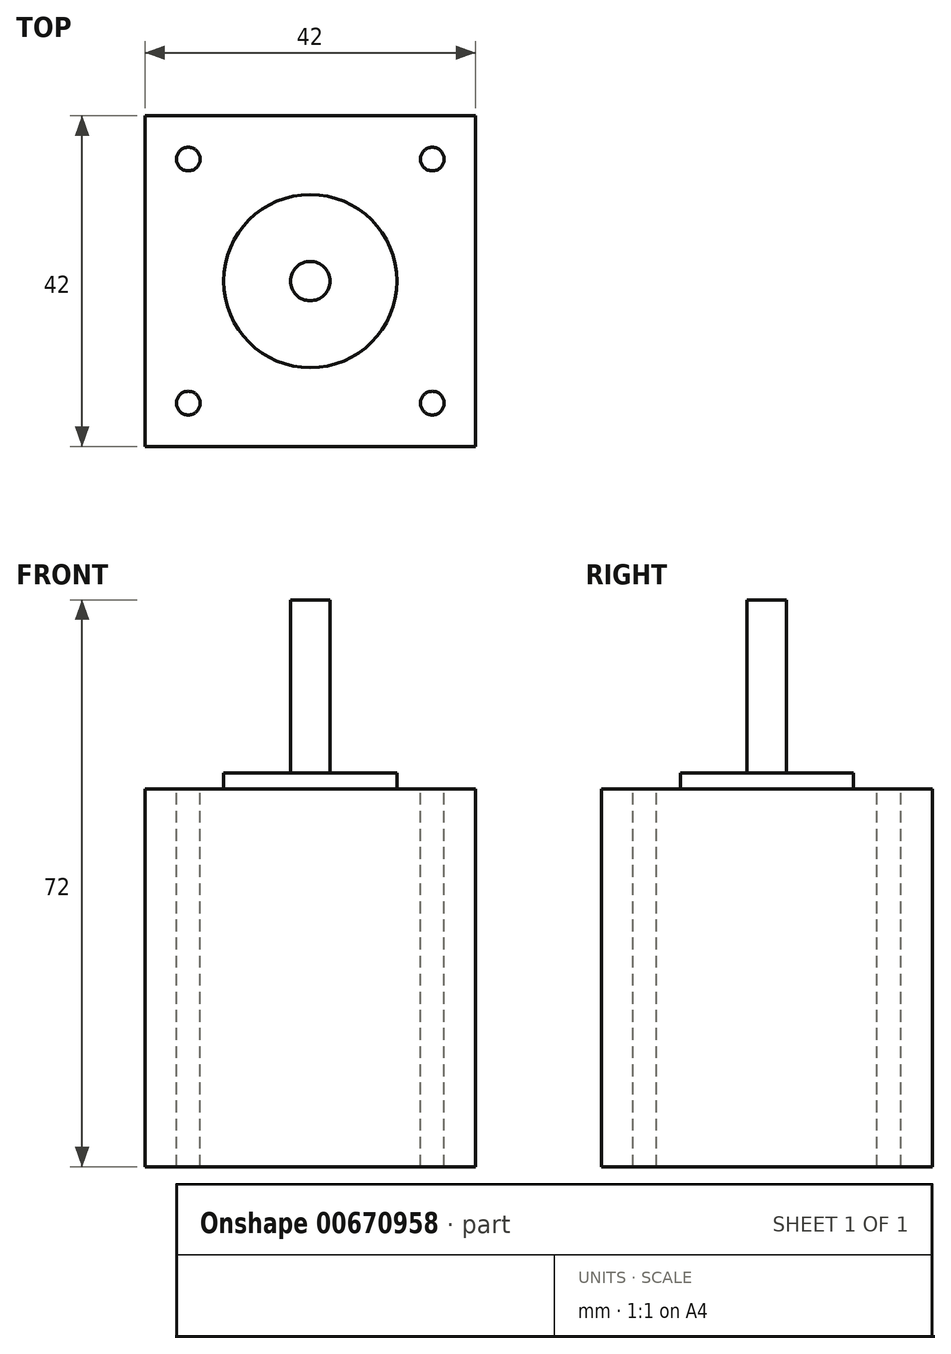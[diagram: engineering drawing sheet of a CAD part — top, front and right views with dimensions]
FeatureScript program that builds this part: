
annotation { "Feature Type Name" : "Feature", "Feature Type Description" : "" }
export const myFeature = defineFeature(function(context is Context, id is Id, definition is map)
    precondition{}
    {
        {
            var Q0;
            Q0=qCreatedBy(makeId("Top.planeOp"),FACE);
            var sketch = newSketch(context, id + "F0", { "sketchPlane" : qUnion([Q0])});
            skLineSegment(sketch, "E0.bottom", {"start": v(21, -21) * mm, "end": v(-21, -21) * mm});
            skLineSegment(sketch, "E0.top", {"start": v(21, 21) * mm, "end": v(-21, 21) * mm});
            skLineSegment(sketch, "E0.left", {"start": v(21, -21) * mm, "end": v(21, 21) * mm});
            skLineSegment(sketch, "E0.right", {"start": v(-21, -21) * mm, "end": v(-21, 21) * mm});
            skPoint(sketch, "E0.middle", {"position": v(0, 0) * mm});
            skLineSegment(sketch, "E1.bottom", {"start": v(15.5, -15.5) * mm, "end": v(-15.5, -15.5) * mm, "construction": true});
            skLineSegment(sketch, "E1.top", {"start": v(15.5, 15.5) * mm, "end": v(-15.5, 15.5) * mm, "construction": true});
            skLineSegment(sketch, "E1.left", {"start": v(15.5, -15.5) * mm, "end": v(15.5, 15.5) * mm, "construction": true});
            skLineSegment(sketch, "E1.right", {"start": v(-15.5, -15.5) * mm, "end": v(-15.5, 15.5) * mm, "construction": true});
            skCircle(sketch, "E2", {"center": v(15.5, 15.5) * mm, "radius": 1.5 * mm});
            skCircle(sketch, "E3", {"center": v(-15.5, 15.5) * mm, "radius": 1.5 * mm});
            skCircle(sketch, "E4", {"center": v(15.5, -15.5) * mm, "radius": 1.5 * mm});
            skCircle(sketch, "E5", {"center": v(-15.5, -15.5) * mm, "radius": 1.5 * mm});
            skCircle(sketch, "E6", {"center": v(0, 0) * mm, "radius": 11 * mm});
            skSolve(sketch);
        }
        {
            var Q0;
            Q0=makeQuery(id+"F0.imprint","IMPRINT",FACE,{"disambiguationData":[TD([[makeQuery(id+"F0.imprint","IMPRINT",EDGE,{"derivedFrom":sQuery(id+"F0.wireOp",EDGE,"E6")}),1.0]])]});
            var Q1;
            Q1=makeQuery(id+"F0.imprint","IMPRINT",FACE,{"disambiguationData":[TD([[makeQuery(id+"F0.imprint","IMPRINT",EDGE,{"derivedFrom":sQuery(id+"F0.wireOp",EDGE,"E0.bottom")}),-1.0]])]});
            extrude(context, id + "F1", {"entities" : qUnion([Q0, Q1]), "oppositeDirection" : true, "depth" : 48 * mm, "offsetDistance" : 25 * mm});
        }
        {
            var Q0;
            Q0=makeQuery(id+"F0.imprint","IMPRINT",FACE,{"disambiguationData":[TD([[makeQuery(id+"F0.imprint","IMPRINT",EDGE,{"derivedFrom":sQuery(id+"F0.wireOp",EDGE,"E6")}),1.0]])]});
            extrude(context, id + "F2", {"entities" : qUnion([Q0]), "operationType" : NewBodyOperationType.ADD, "depth" : 2 * mm, "offsetDistance" : 25 * mm});
        }
        {
            var Q0;
            Q0=makeQuery(id+"F2.opExtrude","CAP_FACE",FACE,{"disambiguationData":[OSD([sQuery(id+"F0.wireOp",EDGE,"E6")])],"isStart":false});
            var sketch = newSketch(context, id + "F3", { "sketchPlane" : qUnion([Q0])});
            skPoint(sketch, "E7.0", {"position": v(0, 0) * mm});
            skCircle(sketch, "E8", {"center": v(0, 0) * mm, "radius": 2.5 * mm});
            skSolve(sketch);
        }
        {
            var Q0;
            Q0 = qSketchRegion(id + "F3", true);
            extrude(context, id + "F4", {"entities" : qUnion([Q0]), "operationType" : NewBodyOperationType.ADD, "depth" : 22 * mm, "offsetDistance" : 25 * mm});
        }
    });
